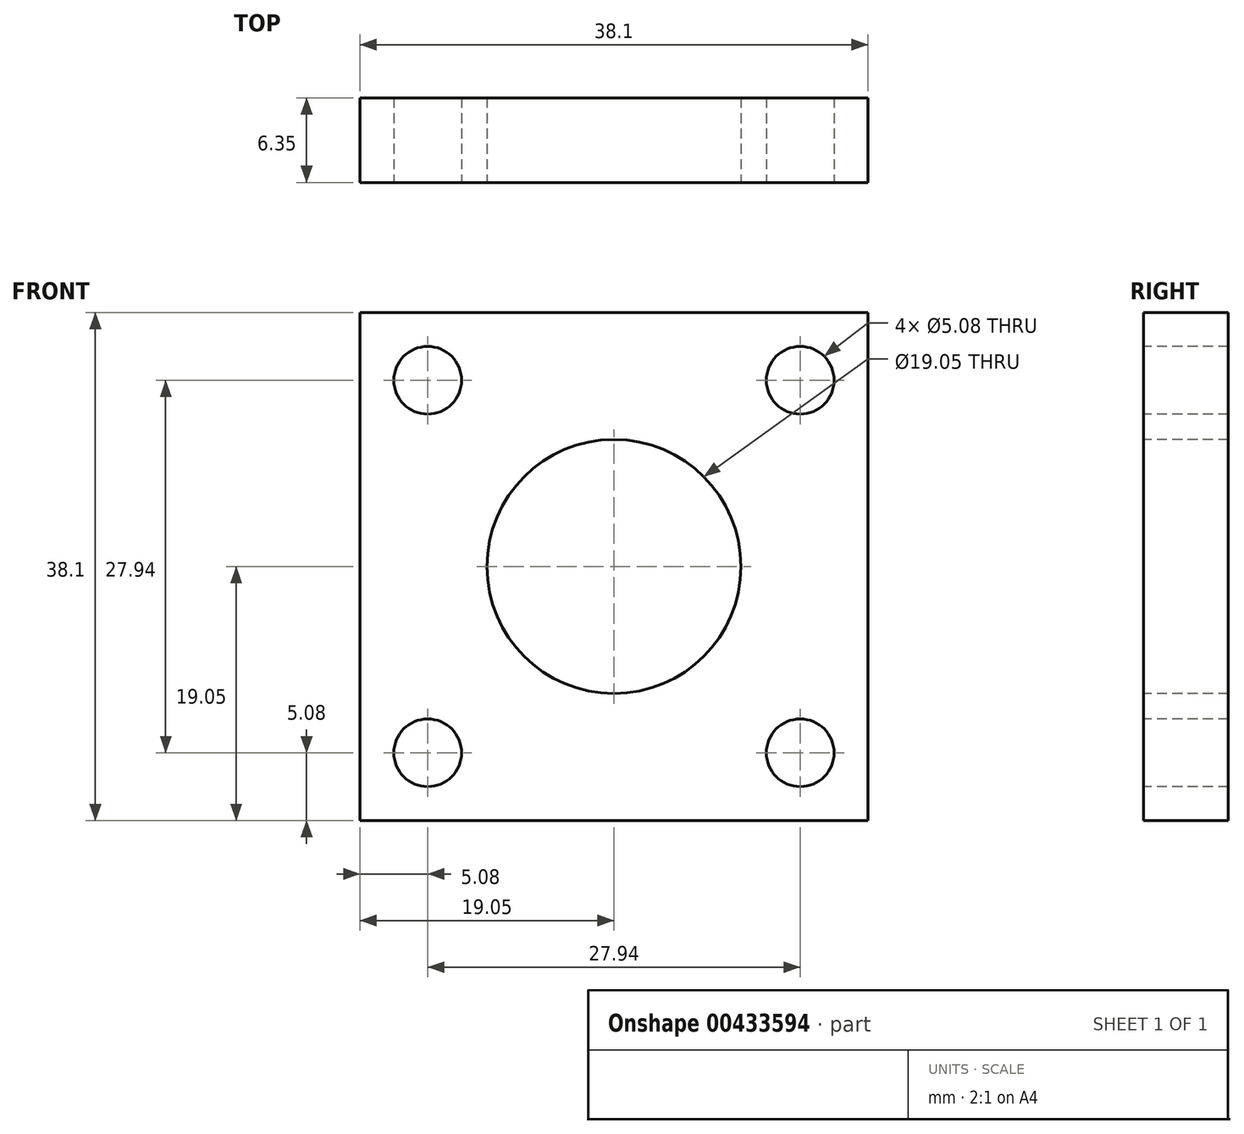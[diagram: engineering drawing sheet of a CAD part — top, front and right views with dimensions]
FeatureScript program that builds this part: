
annotation { "Feature Type Name" : "Feature", "Feature Type Description" : "" }
export const myFeature = defineFeature(function(context is Context, id is Id, definition is map)
    precondition{}
    {
        {
            var Q0;
            Q0=qCreatedBy(makeId("Front.planeOp"),FACE);
            var sketch = newSketch(context, id + "F0", { "sketchPlane" : qUnion([Q0])});
            skLineSegment(sketch, "E0.bottom", {"start": v(-19.05, 19.05) * mm, "end": v(19.05, 19.05) * mm});
            skLineSegment(sketch, "E0.top", {"start": v(-19.05, -19.05) * mm, "end": v(19.05, -19.05) * mm});
            skLineSegment(sketch, "E0.left", {"start": v(-19.05, 19.05) * mm, "end": v(-19.05, -19.05) * mm});
            skLineSegment(sketch, "E0.right", {"start": v(19.05, 19.05) * mm, "end": v(19.05, -19.05) * mm});
            skPoint(sketch, "E0.middle", {"position": v(0, 0) * mm});
            skSolve(sketch);
        }
        {
            var Q0;
            Q0=makeQuery(id+"F0.imprint","IMPRINT",FACE,{"disambiguationData":[TD([[makeQuery(id+"F0.imprint","IMPRINT",EDGE,{"derivedFrom":sQuery(id+"F0.wireOp",EDGE,"E0.bottom")}),-1.0]])]});
            extrude(context, id + "F1", {"entities" : qUnion([Q0]), "depth" : 6.35 * mm});
        }
        {
            var Q0;
            Q0=makeQuery(id+"F1.opExtrude","CAP_FACE",FACE,{"disambiguationData":[OSD([sQuery(id+"F0.wireOp",EDGE,"E0.bottom"),sQuery(id+"F0.wireOp",EDGE,"E0.top"),sQuery(id+"F0.wireOp",EDGE,"E0.left"),sQuery(id+"F0.wireOp",EDGE,"E0.right")])],"isStart":false});
            var sketch = newSketch(context, id + "F2", { "sketchPlane" : qUnion([Q0])});
            skCircle(sketch, "E1", {"center": v(-13.97, 13.97) * mm, "radius": 2.54 * mm});
            skCircle(sketch, "E2", {"center": v(-13.97, -13.97) * mm, "radius": 2.54 * mm});
            skCircle(sketch, "E3", {"center": v(13.97, -13.97) * mm, "radius": 2.54 * mm});
            skCircle(sketch, "E4", {"center": v(13.97, 13.97) * mm, "radius": 2.54 * mm});
            skSolve(sketch);
        }
        {
            var Q0;
            Q0=makeQuery(id+"F2.imprint","IMPRINT",FACE,{"disambiguationData":[TD([[makeQuery(id+"F2.imprint","IMPRINT",EDGE,{"derivedFrom":sQuery(id+"F2.wireOp",EDGE,"E1")}),1.0]])]});
            var Q1;
            Q1=makeQuery(id+"F2.imprint","IMPRINT",FACE,{"disambiguationData":[TD([[makeQuery(id+"F2.imprint","IMPRINT",EDGE,{"derivedFrom":sQuery(id+"F2.wireOp",EDGE,"E4")}),1.0]])]});
            var Q2;
            Q2=makeQuery(id+"F2.imprint","IMPRINT",FACE,{"disambiguationData":[TD([[makeQuery(id+"F2.imprint","IMPRINT",EDGE,{"derivedFrom":sQuery(id+"F2.wireOp",EDGE,"E3")}),1.0]])]});
            var Q3;
            Q3=makeQuery(id+"F2.imprint","IMPRINT",FACE,{"disambiguationData":[TD([[makeQuery(id+"F2.imprint","IMPRINT",EDGE,{"derivedFrom":sQuery(id+"F2.wireOp",EDGE,"E2")}),1.0]])]});
            extrude(context, id + "F3", {"entities" : qUnion([Q0, Q1, Q2, Q3]), "operationType" : NewBodyOperationType.REMOVE, "endBound" : BoundingType.THROUGH_ALL, "oppositeDirection" : true, "depth" : 25.4 * mm});
        }
        {
            var Q0;
            Q0=makeQuery(id+"F1.opExtrude","CAP_FACE",FACE,{"disambiguationData":[OSD([sQuery(id+"F0.wireOp",EDGE,"E0.bottom"),sQuery(id+"F0.wireOp",EDGE,"E0.top"),sQuery(id+"F0.wireOp",EDGE,"E0.left"),sQuery(id+"F0.wireOp",EDGE,"E0.right")])],"isStart":false});
            var sketch = newSketch(context, id + "F4", { "sketchPlane" : qUnion([Q0])});
            skCircle(sketch, "E5", {"center": v(0, 0) * mm, "radius": 9.53 * mm});
            skSolve(sketch);
        }
        {
            var Q0;
            Q0=makeQuery(id+"F4.imprint","IMPRINT",FACE,{"disambiguationData":[TD([[makeQuery(id+"F4.imprint","IMPRINT",EDGE,{"derivedFrom":sQuery(id+"F4.wireOp",EDGE,"E5")}),1.0]])]});
            extrude(context, id + "F5", {"entities" : qUnion([Q0]), "operationType" : NewBodyOperationType.REMOVE, "endBound" : BoundingType.THROUGH_ALL, "oppositeDirection" : true, "depth" : 25.4 * mm});
        }
    });
